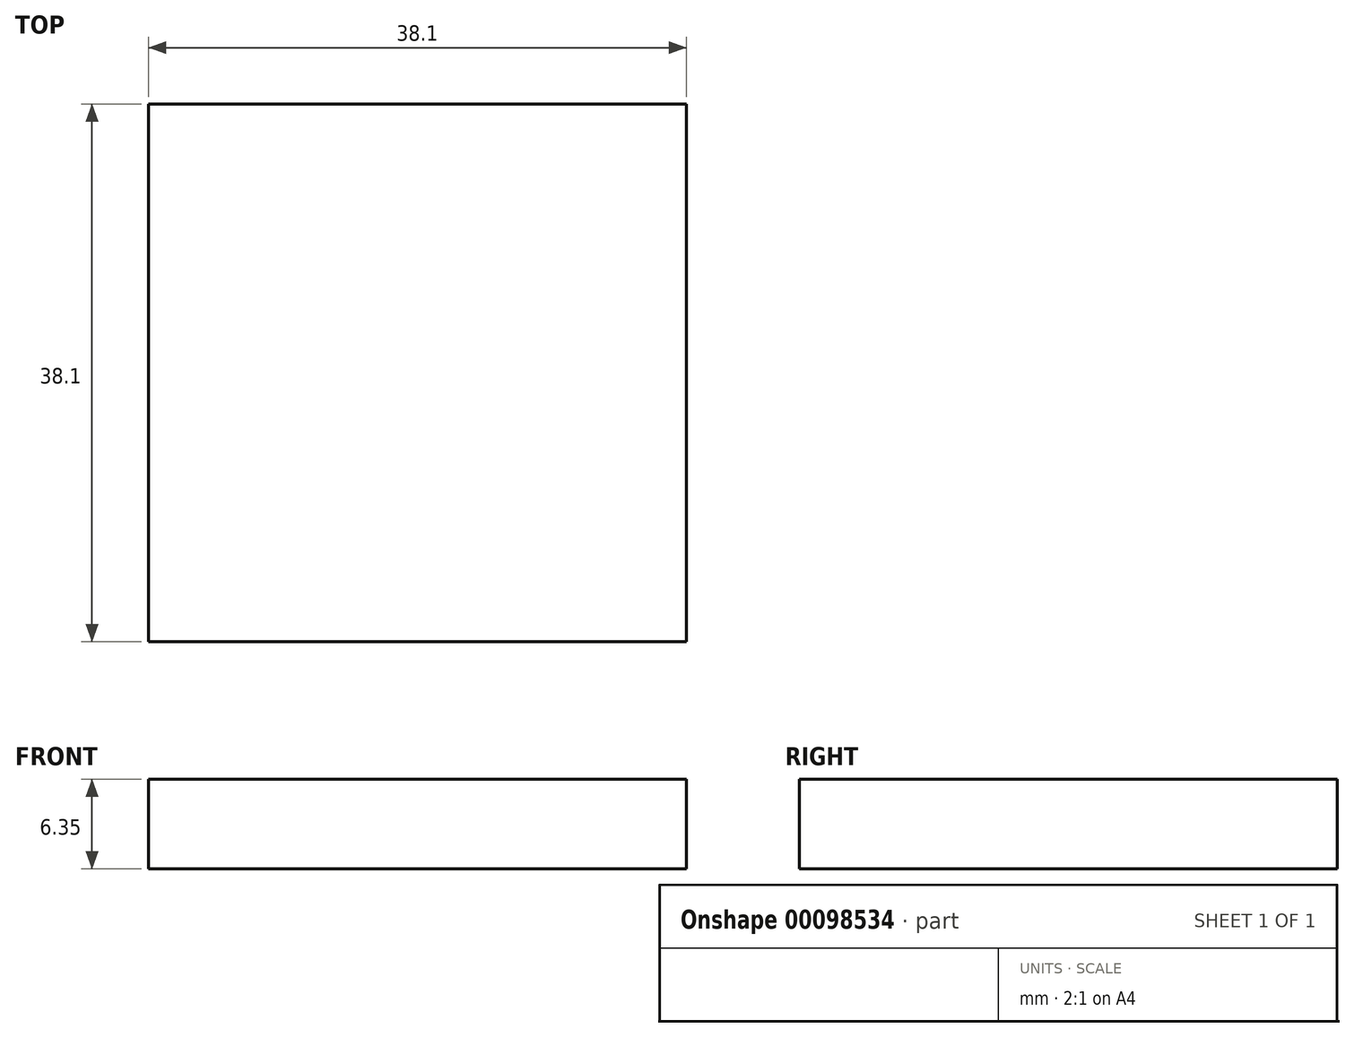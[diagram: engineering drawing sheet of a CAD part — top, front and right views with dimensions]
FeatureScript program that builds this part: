
annotation { "Feature Type Name" : "Feature", "Feature Type Description" : "" }
export const myFeature = defineFeature(function(context is Context, id is Id, definition is map)
    precondition{}
    {
        {
            var Q0;
            Q0=qCreatedBy(makeId("Top.planeOp"),FACE);
            var sketch = newSketch(context, id + "F0", { "sketchPlane" : qUnion([Q0])});
            skLineSegment(sketch, "E0.bottom", {"start": v(19.05, -19.05) * mm, "end": v(-19.05, -19.05) * mm});
            skLineSegment(sketch, "E0.top", {"start": v(19.05, 19.05) * mm, "end": v(-19.05, 19.05) * mm});
            skLineSegment(sketch, "E0.left", {"start": v(19.05, -19.05) * mm, "end": v(19.05, 19.05) * mm});
            skLineSegment(sketch, "E0.right", {"start": v(-19.05, -19.05) * mm, "end": v(-19.05, 19.05) * mm});
            skPoint(sketch, "E0.middle", {"position": v(0, 0) * mm});
            skSolve(sketch);
        }
        {
            var Q0;
            Q0 = qSketchRegion(id + "F0", true);
            extrude(context, id + "F1", {"entities" : qUnion([Q0]), "depth" : 6.35 * mm});
        }
    });
